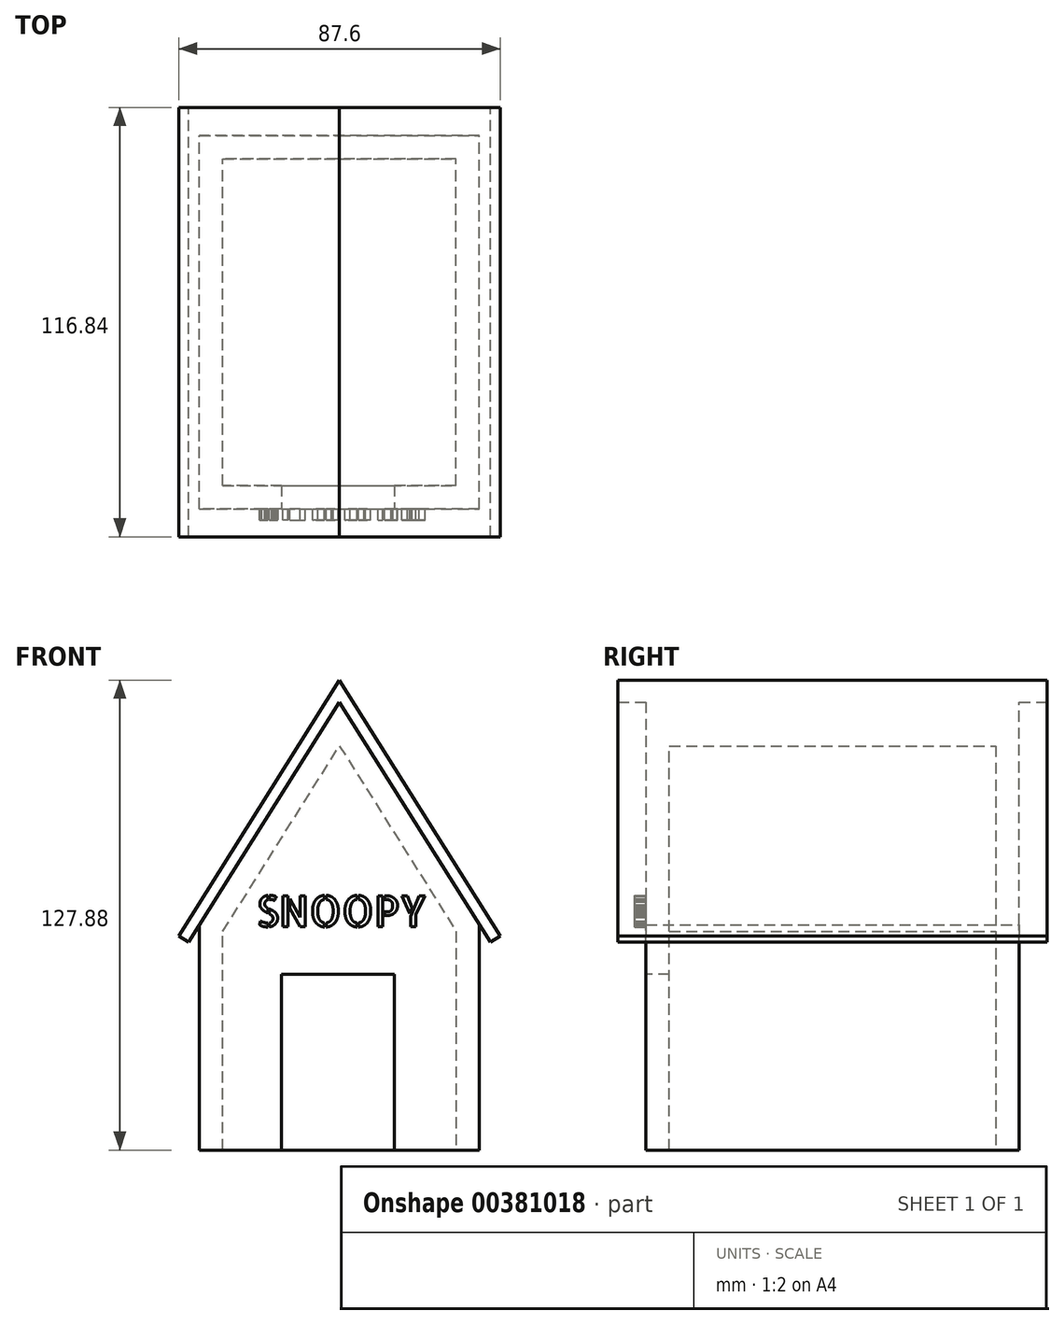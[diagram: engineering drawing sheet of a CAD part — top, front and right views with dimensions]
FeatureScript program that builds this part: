
annotation { "Feature Type Name" : "Feature", "Feature Type Description" : "" }
export const myFeature = defineFeature(function(context is Context, id is Id, definition is map)
    precondition{}
    {
        {
            var Q0;
            Q0=qCreatedBy(makeId("Front.planeOp"),FACE);
            var sketch = newSketch(context, id + "F0", { "sketchPlane" : qUnion([Q0])});
            skLineSegment(sketch, "E0", {"start": v(0, 0) * mm, "end": v(-38.1, 0) * mm});
            skLineSegment(sketch, "E1", {"start": v(-38.1, 0) * mm, "end": v(-38.1, 30.67) * mm});
            skLineSegment(sketch, "E2", {"start": v(-38.1, 30.67) * mm, "end": v(-19.05, 60.96) * mm});
            skLineSegment(sketch, "E3", {"start": v(-19.05, 60.96) * mm, "end": v(0, 30.67) * mm});
            skLineSegment(sketch, "E4", {"start": v(0, 30.67) * mm, "end": v(0, 0) * mm});
            skLineSegment(sketch, "E5", {"start": v(-19.05, 60.96) * mm, "end": v(-19.05, 0) * mm, "construction": true});
            skLineSegment(sketch, "E6", {"start": v(0, 30.67) * mm, "end": v(-38.1, 30.67) * mm, "construction": true});
            skSolve(sketch);
        }
        {
            var Q0;
            Q0=makeQuery(id+"F0.imprint","IMPRINT",FACE,{"disambiguationData":[TD([[makeQuery(id+"F0.imprint","IMPRINT",EDGE,{"derivedFrom":sQuery(id+"F0.wireOp",EDGE,"E0")}),-1.0]])]});
            extrude(context, id + "F1", {"entities" : qUnion([Q0]), "depth" : 50.8 * mm});
        }
        {
            var Q0;
            Q0=makeQuery(id+"F1.opExtrude","CAP_FACE",FACE,{"disambiguationData":[OSD([sQuery(id+"F0.wireOp",EDGE,"E0"),sQuery(id+"F0.wireOp",EDGE,"E1"),sQuery(id+"F0.wireOp",EDGE,"E2"),sQuery(id+"F0.wireOp",EDGE,"E3"),sQuery(id+"F0.wireOp",EDGE,"E4")])],"isStart":false});
            var sketch = newSketch(context, id + "F2", { "sketchPlane" : qUnion([Q0])});
            skSolve(sketch);
        }
        {
            var Q0;
            Q0=makeQuery(id+"F1.opExtrude","SWEPT_FACE",FACE,{"disambiguationData":[OSD([sQuery(id+"F0.wireOp",EDGE,"E0")])]});
            shell(context, id + "F3", {"entities" : qUnion([Q0]), "thickness" : 3.17 * mm});
        }
        {
            var Q0;
            Q0=makeQuery(id+"F2.imprint","IMPRINT",FACE,{"disambiguationData":[TD([[makeQuery(id+"F2.imprint","IMPRINT",EDGE,{"derivedFrom":makeQuery(id+"F1.opExtrude","CAP_EDGE",EDGE,{"disambiguationData":[OSD([sQuery(id+"F0.wireOp",EDGE,"E0")])],"isStart":false})}),-1.0]])]});
            var sketch = newSketch(context, id + "F4", { "sketchPlane" : qUnion([Q0])});
            skLineSegment(sketch, "E7.bottom", {"start": v(-26.92, 0) * mm, "end": v(-11.57, 0) * mm});
            skLineSegment(sketch, "E7.top", {"start": v(-26.92, 23.89) * mm, "end": v(-11.57, 23.89) * mm});
            skLineSegment(sketch, "E7.left", {"start": v(-26.92, 0) * mm, "end": v(-26.92, 23.89) * mm});
            skLineSegment(sketch, "E7.right", {"start": v(-11.57, 0) * mm, "end": v(-11.57, 23.89) * mm});
            skSolve(sketch);
        }
        {
            var Q0;
            Q0 = qSketchRegion(id + "F4", true);
            extrude(context, id + "F5", {"entities" : qUnion([Q0]), "operationType" : NewBodyOperationType.REMOVE, "oppositeDirection" : true, "depth" : 25.4 * mm});
        }
        {
            var Q0;
            Q0=makeQuery(id+"F2.imprint","IMPRINT",FACE,{"disambiguationData":[TD([[makeQuery(id+"F2.imprint","IMPRINT",EDGE,{"derivedFrom":makeQuery(id+"F1.opExtrude","CAP_EDGE",EDGE,{"disambiguationData":[OSD([sQuery(id+"F0.wireOp",EDGE,"E0")])],"isStart":false})}),-1.0]])]});
            var sketch = newSketch(context, id + "F6", { "sketchPlane" : qUnion([Q0])});
            skText(sketch, "E8", { "text": "SNOOPY", "fontName": "AllertaStencil-Regular.ttf"});
            const initialGuessF6  = {"E8": [-0.03039, 0.03037, 1, 0, 0.00423]};
            skSetInitialGuess(sketch, initialGuessF6);
            skSolve(sketch);
        }
        {
            var Q0;
            Q0 = qSketchRegion(id + "F6", true);
            extrude(context, id + "F7", {"entities" : qUnion([Q0]), "operationType" : NewBodyOperationType.ADD, "depth" : 1.52 * mm});
        }
        {
            var Q0;
            Q0=makeQuery(id+"F1.opExtrude","SWEPT_BODY",BODY,{"disambiguationData":[OSD([sQuery(id+"F0.wireOp",EDGE,"E0"),sQuery(id+"F0.wireOp",EDGE,"E1"),sQuery(id+"F0.wireOp",EDGE,"E2"),sQuery(id+"F0.wireOp",EDGE,"E3"),sQuery(id+"F0.wireOp",EDGE,"E4")])]});
            var Q1;
            Q1=qCreatedBy(makeId("Origin.pointOp"),VERTEX);
            transform(context, id + "F8", {"entities" : qUnion([Q0]), "transformType" : TransformType.SCALE_UNIFORMLY, "scale" : 2, "scalePoint" : qUnion([Q1]), "makeCopy" : false});
        }
        {
            var Q0;
            Q0=makeQuery(id+"F1.opExtrude","CAP_FACE",FACE,{"disambiguationData":[OSD([sQuery(id+"F0.wireOp",EDGE,"E0"),sQuery(id+"F0.wireOp",EDGE,"E1"),sQuery(id+"F0.wireOp",EDGE,"E2"),sQuery(id+"F0.wireOp",EDGE,"E3"),sQuery(id+"F0.wireOp",EDGE,"E4")])],"isStart":false});
            var sketch = newSketch(context, id + "F9", { "sketchPlane" : qUnion([Q0])});
            skLineSegment(sketch, "E9.0", {"start": v(-76.2, 61.34) * mm, "end": v(-38.1, 121.92) * mm});
            skLineSegment(sketch, "E9.1", {"start": v(-38.1, 121.92) * mm, "end": v(0, 61.34) * mm});
            skLineSegment(sketch, "E10", {"start": v(-76.2, 61.34) * mm, "end": v(-79.21, 56.56) * mm});
            skLineSegment(sketch, "E11", {"start": v(-79.21, 56.56) * mm, "end": v(-81.9, 58.25) * mm});
            skLineSegment(sketch, "E12", {"start": v(-81.9, 58.25) * mm, "end": v(-38.1, 127.88) * mm});
            skLineSegment(sketch, "E13", {"start": v(-38.1, 127.88) * mm, "end": v(5.7, 58.25) * mm});
            skLineSegment(sketch, "E14", {"start": v(5.7, 58.25) * mm, "end": v(3.01, 56.56) * mm});
            skLineSegment(sketch, "E15", {"start": v(3.01, 56.56) * mm, "end": v(0, 61.34) * mm});
            skLineSegment(sketch, "E16", {"start": v(-79.21, 56.56) * mm, "end": v(3.01, 56.56) * mm, "construction": true});
            skSolve(sketch);
        }
        {
            var Q0;
            Q0 = qSketchRegion(id + "F9", true);
            extrude(context, id + "F10", {"entities" : qUnion([Q0]), "operationType" : NewBodyOperationType.ADD, "depth" : 7.62 * mm, "hasSecondDirection" : true, "secondDirectionOppositeDirection" : true, "secondDirectionDepth" : 109.22 * mm});
        }
    });
